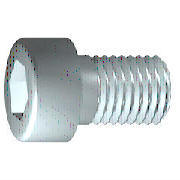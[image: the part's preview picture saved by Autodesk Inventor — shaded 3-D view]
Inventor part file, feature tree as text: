
AUTODESK INVENTOR PART (.ipt)
format: ipt  version: 2025 (Build 290162000, 162)  size: 199,168 bytes
history: native  units: mm (DEFAULTED — no unit token found)
features: extrude x1, plane x1, fillet x1
ambient origin geometry x7: Origin, YZ Plane, XY Plane, X Axis, Y Axis, Z Axis, Center Point
bodies: Solid1 (feature_tree), Body (feature_tree)
feature tree (3):
  extrude  "Slot"  Depth=4.170585mm
  plane  "Work Plane1"
  fillet  "Fillet2"  Radius=0.429515mm
